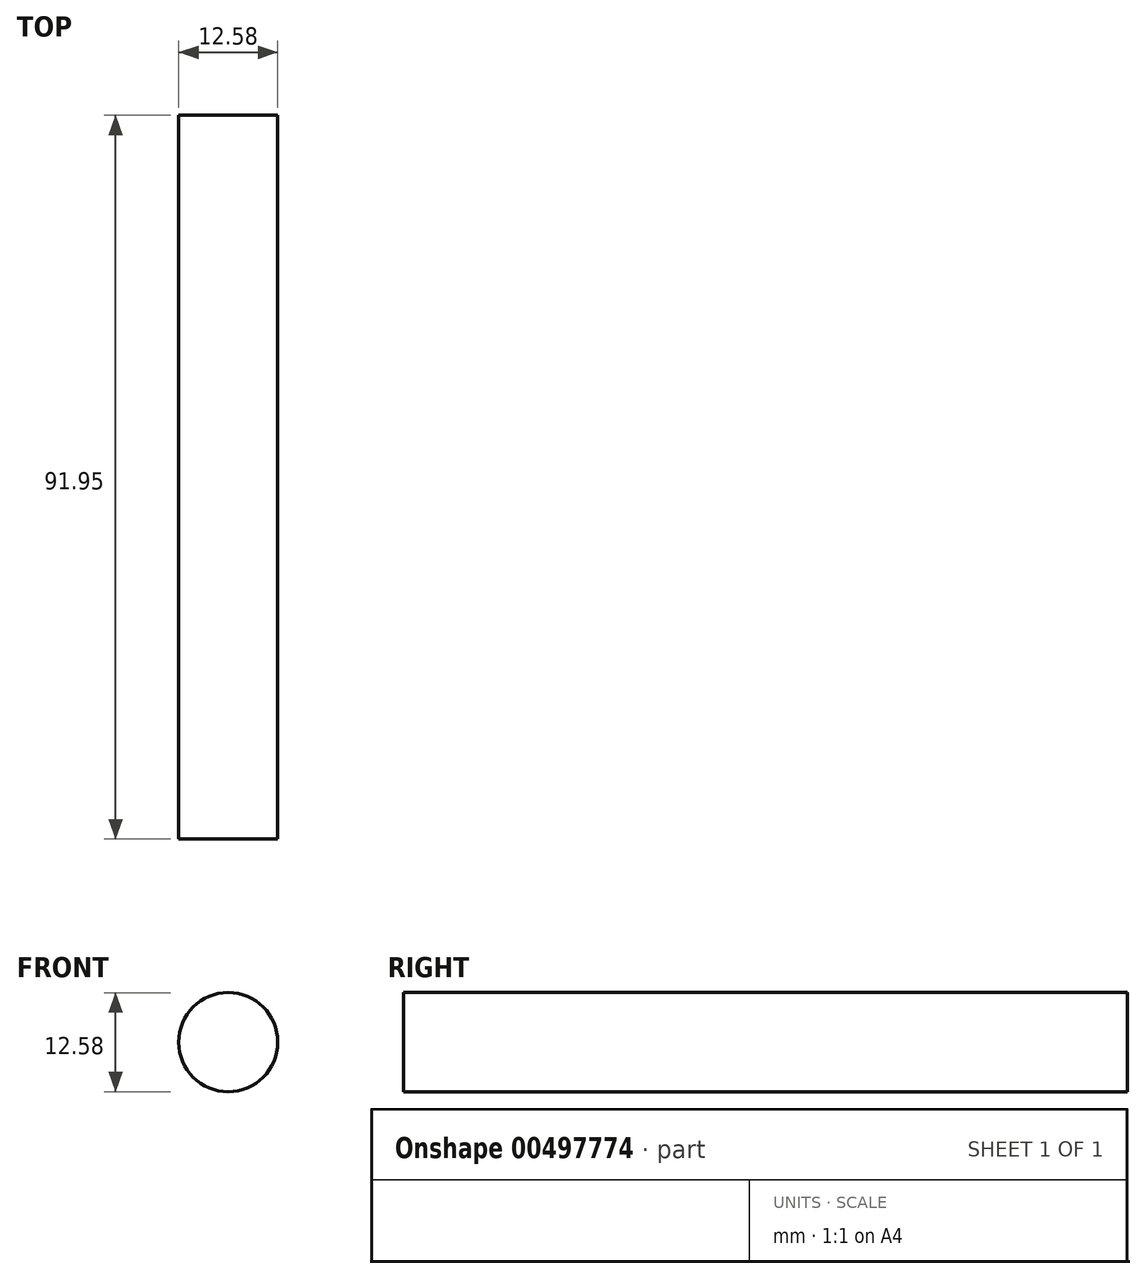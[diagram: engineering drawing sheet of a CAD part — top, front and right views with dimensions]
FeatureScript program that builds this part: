
annotation { "Feature Type Name" : "Feature", "Feature Type Description" : "" }
export const myFeature = defineFeature(function(context is Context, id is Id, definition is map)
    precondition{}
    {
        {
            var Q0;
            Q0=qCreatedBy(makeId("Front.planeOp"),FACE);
            var sketch = newSketch(context, id + "F0", { "sketchPlane" : qUnion([Q0])});
            skCircle(sketch, "E0", {"center": v(0, 0) * mm, "radius": 6.3 * mm});
            skCircle(sketch, "E1", {"center": v(0, 0) * mm, "radius": 4.92 * mm});
            skSolve(sketch);
        }
        {
            var Q0;
            Q0=makeQuery(id+"F0.imprint","IMPRINT",FACE,{"disambiguationData":[TD([[makeQuery(id+"F0.imprint","IMPRINT",EDGE,{"derivedFrom":sQuery(id+"F0.wireOp",EDGE,"E1")}),1.0]])]});
            var Q1;
            Q1=makeQuery(id+"F0.imprint","IMPRINT",FACE,{"disambiguationData":[TD([[makeQuery(id+"F0.imprint","IMPRINT",EDGE,{"derivedFrom":sQuery(id+"F0.wireOp",EDGE,"E0")}),1.0]])]});
            extrude(context, id + "F1", {"entities" : qUnion([Q0, Q1]), "depth" : 91.95 * mm});
        }
    });
